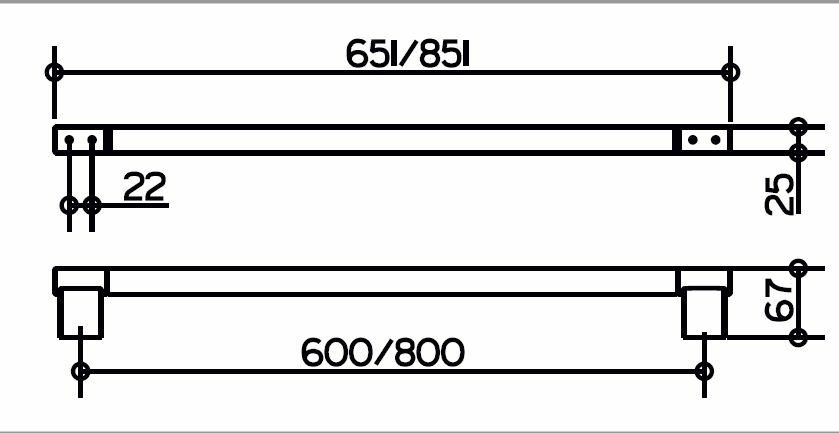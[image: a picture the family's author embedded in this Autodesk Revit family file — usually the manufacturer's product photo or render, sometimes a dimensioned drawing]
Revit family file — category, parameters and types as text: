
# Revit family: KEUCO_34901010300
name_source: partatom
category: Allgemeines Modell
revit_build: Autodesk Revit 2016 (Build: 20150220_1215(x64)
units: mm (PartAtom-declared; Revit-internal decimal feet)

## family parameters
Arbeitsebenenbasiert = Ja
Beim Laden mit Abzugskörper schneiden = Nein
Bemaßung runder Anschluss = Durchmesser verwenden
Gemeinsam genutzt = Nein
Immer vertikal = Nein
Kann Basisbauteil für Bewehrung sein = Nein
Raumberechnungspunkt = Nein
Teiletyp = Normal

## types (18) — shared parameters
Beschreibung = zur waagerechten oder senkrechten Montage
Hersteller = KEUCO
Serie = Plan
URL = https://www.keuco.com
Vorgabe-Ansicht = 1219 mm
zero-valued in all types: Gewicht

## per-type parameters (varying)
| type | Ausschreibungstext | Rail Length | Stange Material |
| 34901010300 | KEUCO PLAN Haltegriff 34901010300
hochglanzverchromter Haltegriff 
in ästhetischem, funktionalem und ergonomischem Design,
zur waagerechten oder senkrechten Montage,
bis 115 kg belastbar, antistatisch, leicht zu reinigen,
Rohrdurchmesser 33 mm, Rosettendurchmesser 82 mm,
Achsmaß 300 mm, Gesamtbreite von 382 mm,
Ausladung 90 mm
Der Haltegriff wird verdeckt angebracht,

Im Lieferumfang enthalten:
Befestigungs-Set 1 Art.-Nr. 34990000100 (je 1 x pro Wandbefestigung)
Der Griff ist Bauart geprüft,
nicht kombinierbar mit Klappsitz mit Rückenlehne

Weitere Befestigungs-Sets
(je nach Ankergrund/Mauerwerk):
Befestigungs-Set 4 (Art.-Nr. 34990000200) oder
Befestigungs-Set 7 (Art.-Nr. 34993000200)

Bitte zusätzlich bestellen
(jeweils 1x pro Wandhalterung) | 382 mm  [stored 1.25328 ft] | Verchromt |
| 34901010400 | KEUCO PLAN CARE Haltegriff 34901010400
hochglanzverchromter Haltegriff 
in ästhetischem, funktionalem und ergonomischem Design,
zur waagerechten oder senkrechten Montage,
bis 115 kg belastbar, antistatisch, leicht zu reinigen,
Rohrdurchmesser 33 mm, Rosettendurchmesser 82 mm,
Achsmaß 400 mm, Gesamtbreite von 482 mm,
Ausladung 90 mm, 
Der Haltegriff wird verdeckt angebracht,

Im Lieferumfang enthalten: 
Befestigungs-Set 1 Art.-Nr. 34990000100 (je 1 x pro Wandbefestigung) 
Der Griff ist Bauart geprüft

Weitere Befestigungs-Sets
(je nach Ankergrund/Mauerwerk):
Befestigungs-Set 4 (Art.-Nr. 34990000200) oder
Befestigungs-Set 7 (Art.-Nr. 34993000200)
Bitte zusätzlich bestellen
(jeweils 1x pro Wandhalterung) | 482 mm  [stored 1.58136 ft] | Verchromt |
| 34901010500 | KEUCO PLAN CARE Haltegriff 34901010500
hochglanzverchromter Haltegriff 
in ästhetischem, funktionalem und ergonomischem Design,
zur waagerechten oder senkrechten Montage,
bis 115 kg belastbar, antistatisch, leicht zu reinigen,
Rohrdurchmesser 33 mm, Rosettendurchmesser 82 mm,
Achsmaß 500 mm, Gesamtbreite von 582 mm,
Ausladung 90 mm, 
Der Haltegriff wird verdeckt angebracht,

Im Lieferumfang enthalten: 
Befestigungs-Set 1 Art.-Nr. 34990000100 (je 1 x pro Wandbefestigung) 
Der Griff ist Bauart geprüft

Weitere Befestigungs-Sets
(je nach Ankergrund/Mauerwerk):
Befestigungs-Set 4 (Art.-Nr. 34990000200) oder
Befestigungs-Set 7 (Art.-Nr. 34993000200)
Bitte zusätzlich bestellen
(jeweils 1x pro Wandhalterung) | 582 mm  [stored 1.90945 ft] | Verchromt |
| 34901010600 | KEUCO PLAN CARE Haltegriff 34901010600
hochglanzverchromter Haltegriff 
in ästhetischem, funktionalem und ergonomischem Design,
zur waagerechten oder senkrechten Montage,
bis 115 kg belastbar, antistatisch, leicht zu reinigen,
Rohrdurchmesser 33 mm, Rosettendurchmesser 82 mm,
Achsmaß 600 mm, Gesamtbreite von 682 mm,
Ausladung 90 mm, 
Der Haltegriff wird verdeckt angebracht,

Im Lieferumfang enthalten: 
Befestigungs-Set 1 Art.-Nr. 34990000100 (je 1 x pro Wandbefestigung) 
Der Griff ist Bauart geprüft

Weitere Befestigungs-Sets
(je nach Ankergrund/Mauerwerk):
Befestigungs-Set 4 (Art.-Nr. 34990000200) oder
Befestigungs-Set 7 (Art.-Nr. 34993000200)
Bitte zusätzlich bestellen
(jeweils 1x pro Wandhalterung) | 682 mm | Verchromt |
| 34901010700 | KEUCO PLAN CARE Haltegriff 34901010700
hochglanzverchromter Haltegriff 
in ästhetischem, funktionalem und ergonomischem Design,
zur waagerechten oder senkrechten Montage,
bis 115 kg belastbar, antistatisch, leicht zu reinigen,
Rohrdurchmesser 33 mm, Rosettendurchmesser 82 mm,
Achsmaß 700 mm, Gesamtbreite von 782 mm,
Ausladung 90 mm, 
Der Haltegriff wird verdeckt angebracht,

Im Lieferumfang enthalten: 
Befestigungs-Set 1 Art.-Nr. 34990000100 (je 1 x pro Wandbefestigung) 
Der Griff ist Bauart geprüft

Weitere Befestigungs-Sets
(je nach Ankergrund/Mauerwerk):
Befestigungs-Set 4 (Art.-Nr. 34990000200) oder
Befestigungs-Set 7 (Art.-Nr. 34993000200)
Bitte zusätzlich bestellen
(jeweils 1x pro Wandhalterung) | 782 mm | Verchromt |
| 34901010800 | KEUCO PLAN CARE Haltegriff 34901010800
hochglanzverchromter Haltegriff 
in ästhetischem, funktionalem und ergonomischem Design,
zur waagerechten oder senkrechten Montage,
bis 115 kg belastbar, antistatisch, leicht zu reinigen,
Rohrdurchmesser 33 mm, Rosettendurchmesser 82 mm,
Achsmaß 800 mm, Gesamtbreite von 882 mm,
Ausladung 90 mm, 
Der Haltegriff wird verdeckt angebracht,

Im Lieferumfang enthalten: 
Befestigungs-Set 1 Art.-Nr. 34990000100 (je 1 x pro Wandbefestigung) 
Der Griff ist Bauart geprüft

Weitere Befestigungs-Sets
(je nach Ankergrund/Mauerwerk):
Befestigungs-Set 4 (Art.-Nr. 34990000200) oder
Befestigungs-Set 7 (Art.-Nr. 34993000200)
Bitte zusätzlich bestellen
(jeweils 1x pro Wandhalterung) | 882 mm  [stored 2.8937 ft] | Verchromt |
| 34901010900 | KEUCO PLAN CARE Haltegriff 34901010900
hochglanzverchromter Haltegriff 
in ästhetischem, funktionalem und ergonomischem Design,
zur waagerechten oder senkrechten Montage,
bis 115 kg belastbar, antistatisch, leicht zu reinigen,
Rohrdurchmesser 33 mm, Rosettendurchmesser 82 mm,
Achsmaß 900 mm, Gesamtbreite von 982 mm,
Ausladung 90 mm, 
Der Haltegriff wird verdeckt angebracht,

Im Lieferumfang enthalten: 
Befestigungs-Set 1 Art.-Nr. 34990000100 (je 1 x pro Wandbefestigung) 
Der Griff ist Bauart geprüft

Weitere Befestigungs-Sets
(je nach Ankergrund/Mauerwerk):
Befestigungs-Set 4 (Art.-Nr. 34990000200) oder
Befestigungs-Set 7 (Art.-Nr. 34993000200)
Bitte zusätzlich bestellen
(jeweils 1x pro Wandhalterung) | 982 mm  [stored 3.22178 ft] | Verchromt |
| 34901011000 | KEUCO PLAN CARE Haltegriff 34901011000
hochglanzverchromter Haltegriff 
in ästhetischem, funktionalem und ergonomischem Design,
zur waagerechten oder senkrechten Montage,
bis 115 kg belastbar, antistatisch, leicht zu reinigen,
Rohrdurchmesser 33 mm, Rosettendurchmesser 82 mm,
Achsmaß 1000 mm, Gesamtbreite von 1082 mm,
Ausladung 90 mm, 
Der Haltegriff wird verdeckt angebracht,

Diese Ausführung ist mit einer
3. Wandbefestigung (mittig) ausgestattet.

Im Lieferumfang enthalten: 
Befestigungs-Set 1 Art.-Nr. 34990000100 (je 1 x pro Wandbefestigung) 
Der Griff ist Bauart geprüft

Weitere Befestigungs-Sets
(je nach Ankergrund/Mauerwerk):
Befestigungs-Set 4 (Art.-Nr. 34990000200) oder
Befestigungs-Set 7 (Art.-Nr. 34993000200)
Bitte zusätzlich bestellen
(jeweils 1x pro Wandhalterung) | 1082 mm  [stored 3.54987 ft] | Verchromt |
| 34901011100 | KEUCO PLAN CARE Haltegriff 34901011100
hochglanzverchromter Haltegriff 
in ästhetischem, funktionalem und ergonomischem Design,
zur waagerechten oder senkrechten Montage,
bis 115 kg belastbar, antistatisch, leicht zu reinigen,
Rohrdurchmesser 33 mm, Rosettendurchmesser 82 mm,
Achsmaß 1100 mm, Gesamtbreite von 1182 mm,
Ausladung 90 mm, 
Der Haltegriff wird verdeckt angebracht,

Diese Ausführung ist mit einer
3. Wandbefestigung (mittig) ausgestattet.

Im Lieferumfang enthalten: 
Befestigungs-Set 1 Art.-Nr. 34990000100 (je 1 x pro Wandbefestigung) 
Der Griff ist Bauart geprüft

Weitere Befestigungs-Sets
(je nach Ankergrund/Mauerwerk):
Befestigungs-Set 4 (Art.-Nr. 34990000200) oder
Befestigungs-Set 7 (Art.-Nr. 34993000200)
Bitte zusätzlich bestellen
(jeweils 1x pro Wandhalterung) | 1182 mm  [stored 3.87795 ft] | Verchromt |
| 34901170300 | KEUCO PLAN Haltegriff 34901170300
Aluminium silber-eloxierter(E6 EV1)/verchromter Haltegriff,
in ästhetischem, funktionalem und ergonomischem Design,
zur waagerechten oder senkrechten Montage,
bis 115 kg belastbar, antistatisch, leicht zu reinigen,
Rohrdurchmesser 33 mm, Rosettendurchmesser 82 mm,
Achsmaß 300 mm, Gesamtbreite von 382 mm,
Ausladung 90 mm
Der Haltegriff wird verdeckt angebracht,

Im Lieferumfang enthalten:
Befestigungs-Set 1 Art.-Nr. 34990000100 (je 1 x pro Wandbefestigung)
Der Griff ist Bauart geprüft,
nicht kombinierbar mit Klappsitz mit Rückenlehne

Weitere Befestigungs-Sets
(je nach Ankergrund/Mauerwerk):
Befestigungs-Set 4 (Art.-Nr. 34990000200) oder
Befestigungs-Set 7 (Art.-Nr. 34993000200)

Bitte zusätzlich bestellen
(jeweils 1x pro Wandhalterung) | 382 mm  [stored 1.25328 ft] | Aluminium silber-eloxiert (E6 EV1) |
| 34901170400 | KEUCO PLAN Haltegriff 34901170400
Aluminium silber-eloxierter(E6 EV1)/verchromter Haltegriff,
in ästhetischem, funktionalem und ergonomischem Design,
zur waagerechten oder senkrechten Montage,
bis 115 kg belastbar, antistatisch, leicht zu reinigen,
Rohrdurchmesser 33 mm, Rosettendurchmesser 82 mm,
Achsmaß 400 mm, Gesamtbreite von 482 mm,
Ausladung 90 mm
Der Haltegriff wird verdeckt angebracht,

Im Lieferumfang enthalten:
Befestigungs-Set 1 Art.-Nr. 34990000100 (je 1 x pro Wandbefestigung)
Der Griff ist Bauart geprüft,

Weitere Befestigungs-Sets
(je nach Ankergrund/Mauerwerk):
Befestigungs-Set 4 (Art.-Nr. 34990000200) oder
Befestigungs-Set 7 (Art.-Nr. 34993000200)

Bitte zusätzlich bestellen
(jeweils 1x pro Wandhalterung) | 482 mm  [stored 1.58136 ft] | Verchromt |
| 34901170500 | KEUCO PLAN Haltegriff 34901170500
Aluminium silber-eloxierter(E6 EV1)/verchromter Haltegriff,
in ästhetischem, funktionalem und ergonomischem Design,
zur waagerechten oder senkrechten Montage,
bis 115 kg belastbar, antistatisch, leicht zu reinigen,
Rohrdurchmesser 33 mm, Rosettendurchmesser 82 mm,
Achsmaß 500 mm, Gesamtbreite von 582 mm,
Ausladung 90 mm
Der Haltegriff wird verdeckt angebracht,

Im Lieferumfang enthalten:
Befestigungs-Set 1 Art.-Nr. 34990000100 (je 1 x pro Wandbefestigung)
Der Griff ist Bauart geprüft,

Weitere Befestigungs-Sets
(je nach Ankergrund/Mauerwerk):
Befestigungs-Set 4 (Art.-Nr. 34990000200) oder
Befestigungs-Set 7 (Art.-Nr. 34993000200)

Bitte zusätzlich bestellen
(jeweils 1x pro Wandhalterung) | 582 mm  [stored 1.90945 ft] | Aluminium silber-eloxiert (E6 EV1) |
| 34901170600 | KEUCO PLAN Haltegriff 34901170600
Aluminium silber-eloxierter(E6 EV1)/verchromter Haltegriff,
in ästhetischem, funktionalem und ergonomischem Design,
zur waagerechten oder senkrechten Montage,
bis 115 kg belastbar, antistatisch, leicht zu reinigen,
Rohrdurchmesser 33 mm, Rosettendurchmesser 82 mm,
Achsmaß 600 mm, Gesamtbreite von 682 mm,
Ausladung 90 mm
Der Haltegriff wird verdeckt angebracht,

Im Lieferumfang enthalten:
Befestigungs-Set 1 Art.-Nr. 34990000100 (je 1 x pro Wandbefestigung)
Der Griff ist Bauart geprüft,

Weitere Befestigungs-Sets
(je nach Ankergrund/Mauerwerk):
Befestigungs-Set 4 (Art.-Nr. 34990000200) oder
Befestigungs-Set 7 (Art.-Nr. 34993000200)

Bitte zusätzlich bestellen
(jeweils 1x pro Wandhalterung) | 682 mm | Aluminium silber-eloxiert (E6 EV1) |
| 34901170700 | KEUCO PLAN Haltegriff 34901170700
Aluminium silber-eloxierter(E6 EV1)/verchromter Haltegriff,
in ästhetischem, funktionalem und ergonomischem Design,
zur waagerechten oder senkrechten Montage,
bis 115 kg belastbar, antistatisch, leicht zu reinigen,
Rohrdurchmesser 33 mm, Rosettendurchmesser 82 mm,
Achsmaß 700 mm, Gesamtbreite von 582 mm,
Ausladung 90 mm
Der Haltegriff wird verdeckt angebracht,

Im Lieferumfang enthalten:
Befestigungs-Set 1 Art.-Nr. 34990000100 (je 1 x pro Wandbefestigung)
Der Griff ist Bauart geprüft,

Weitere Befestigungs-Sets
(je nach Ankergrund/Mauerwerk):
Befestigungs-Set 4 (Art.-Nr. 34990000200) oder
Befestigungs-Set 7 (Art.-Nr. 34993000200)

Bitte zusätzlich bestellen
(jeweils 1x pro Wandhalterung) | 782 mm | Aluminium silber-eloxiert (E6 EV1) |
| 34901170800 | KEUCO PLAN Haltegriff 34901170800
Aluminium silber-eloxierter(E6 EV1)/verchromter Haltegriff,
in ästhetischem, funktionalem und ergonomischem Design,
zur waagerechten oder senkrechten Montage,
bis 115 kg belastbar, antistatisch, leicht zu reinigen,
Rohrdurchmesser 33 mm, Rosettendurchmesser 82 mm,
Achsmaß 800 mm, Gesamtbreite von 882 mm,
Ausladung 90 mm
Der Haltegriff wird verdeckt angebracht,

Im Lieferumfang enthalten:
Befestigungs-Set 1 Art.-Nr. 34990000100 (je 1 x pro Wandbefestigung)
Der Griff ist Bauart geprüft,

Weitere Befestigungs-Sets
(je nach Ankergrund/Mauerwerk):
Befestigungs-Set 4 (Art.-Nr. 34990000200) oder
Befestigungs-Set 7 (Art.-Nr. 34993000200)

Bitte zusätzlich bestellen
(jeweils 1x pro Wandhalterung) | 882 mm  [stored 2.8937 ft] | Aluminium silber-eloxiert (E6 EV1) |
| 34901170900 | KEUCO PLAN Haltegriff 34901170900
Aluminium silber-eloxierter(E6 EV1)/verchromter Haltegriff,
in ästhetischem, funktionalem und ergonomischem Design,
zur waagerechten oder senkrechten Montage,
bis 115 kg belastbar, antistatisch, leicht zu reinigen,
Rohrdurchmesser 33 mm, Rosettendurchmesser 82 mm,
Achsmaß 900 mm, Gesamtbreite von 982 mm,
Ausladung 90 mm
Der Haltegriff wird verdeckt angebracht,

Im Lieferumfang enthalten:
Befestigungs-Set 1 Art.-Nr. 34990000100 (je 1 x pro Wandbefestigung)
Der Griff ist Bauart geprüft,

Weitere Befestigungs-Sets
(je nach Ankergrund/Mauerwerk):
Befestigungs-Set 4 (Art.-Nr. 34990000200) oder
Befestigungs-Set 7 (Art.-Nr. 34993000200)

Bitte zusätzlich bestellen
(jeweils 1x pro Wandhalterung) | 982 mm  [stored 3.22178 ft] | Aluminium silber-eloxiert (E6 EV1) |
| 34901171000 | KEUCO PLAN Haltegriff 34901171000
Aluminium silber-eloxierter(E6 EV1)/verchromter Haltegriff,
in ästhetischem, funktionalem und ergonomischem Design,
zur waagerechten oder senkrechten Montage,
bis 115 kg belastbar, antistatisch, leicht zu reinigen,
Rohrdurchmesser 33 mm, Rosettendurchmesser 82 mm,
Achsmaß 1000 mm, Gesamtbreite von 1082 mm,
Ausladung 90 mm
Der Haltegriff wird verdeckt angebracht,

Diese Ausführung ist mit einer
3. Wandbefestigung (mittig) ausgestattet.

Im Lieferumfang enthalten:
Befestigungs-Set 1 Art.-Nr. 34990000100 (je 1 x pro Wandbefestigung)
Der Griff ist Bauart geprüft,

Weitere Befestigungs-Sets
(je nach Ankergrund/Mauerwerk):
Befestigungs-Set 4 (Art.-Nr. 34990000200) oder
Befestigungs-Set 7 (Art.-Nr. 34993000200)

Bitte zusätzlich bestellen
(jeweils 1x pro Wandhalterung) | 1082 mm  [stored 3.54987 ft] | Aluminium silber-eloxiert (E6 EV1) |
| 34901171100 | KEUCO PLAN Haltegriff 34901171100
Aluminium silber-eloxierter(E6 EV1)/verchromter Haltegriff,
in ästhetischem, funktionalem und ergonomischem Design,
zur waagerechten oder senkrechten Montage,
bis 115 kg belastbar, antistatisch, leicht zu reinigen,
Rohrdurchmesser 33 mm, Rosettendurchmesser 82 mm,
Achsmaß 1100 mm, Gesamtbreite von 1182 mm,
Ausladung 90 mm
Der Haltegriff wird verdeckt angebracht,

Diese Ausführung ist mit einer
3. Wandbefestigung (mittig) ausgestattet.

Im Lieferumfang enthalten:
Befestigungs-Set 1 Art.-Nr. 34990000100 (je 1 x pro Wandbefestigung)
Der Griff ist Bauart geprüft,

Weitere Befestigungs-Sets
(je nach Ankergrund/Mauerwerk):
Befestigungs-Set 4 (Art.-Nr. 34990000200) oder
Befestigungs-Set 7 (Art.-Nr. 34993000200)

Bitte zusätzlich bestellen
(jeweils 1x pro Wandhalterung) | 1182 mm  [stored 3.87795 ft] | Aluminium silber-eloxiert (E6 EV1) |

note: column(s) folded — value = type name in every type: Artikelnummer

note: [stored X ft] marks values corroborated as IEEE doubles in the binary element streams (Revit-internal decimal feet)

## geometry (parser evidence)
native form markers: Sweep x3
no freeform markers — native parametric forms only
